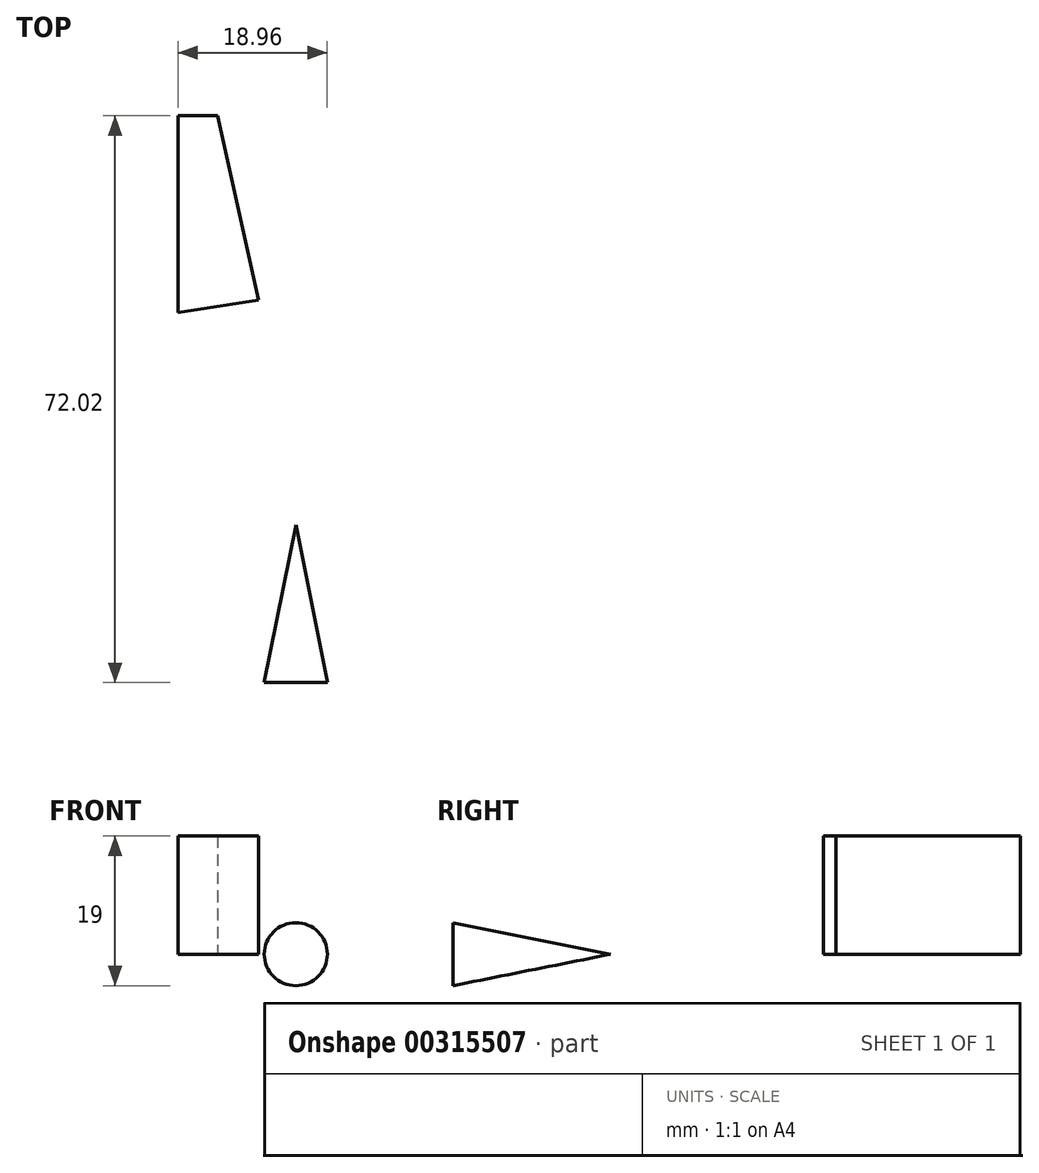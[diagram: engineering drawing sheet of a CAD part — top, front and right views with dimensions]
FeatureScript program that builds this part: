
annotation { "Feature Type Name" : "Feature", "Feature Type Description" : "" }
export const myFeature = defineFeature(function(context is Context, id is Id, definition is map)
    precondition{}
    {
        {
            var Q0;
            Q0=qCreatedBy(makeId("Top.planeOp"),FACE);
            var sketch = newSketch(context, id + "F0", { "sketchPlane" : qUnion([Q0])});
            skLineSegment(sketch, "E0", {"start": v(-41.16, -17.84) * mm, "end": v(-37.16, -17.84) * mm});
            skLineSegment(sketch, "E1", {"start": v(-37.16, -17.84) * mm, "end": v(-37.16, 2.16) * mm});
            skLineSegment(sketch, "E2", {"start": v(-37.16, 2.16) * mm, "end": v(-41.16, -17.84) * mm});
            skSolve(sketch);
        }
        {
            var Q0;
            Q0=makeQuery(id+"F0.imprint","IMPRINT",FACE,{"disambiguationData":[TD([[makeQuery(id+"F0.imprint","IMPRINT",EDGE,{"derivedFrom":sQuery(id+"F0.wireOp",EDGE,"E0")}),1.0]])]});
            var Q1;
            Q1=sQuery(id+"F0.wireOp",EDGE,"E1");
            revolve(context, id + "F1", {"entities" : qUnion([Q0]), "axis" : qUnion([Q1]), "revolveType" : RevolveType.FULL});
        }
        {
            var Q0;
            Q0=qCreatedBy(makeId("Top.planeOp"),FACE);
            var sketch = newSketch(context, id + "F2", { "sketchPlane" : qUnion([Q0])});
            skLineSegment(sketch, "E3", {"start": v(-52.12, 54.18) * mm, "end": v(-52.12, 29.18) * mm});
            skLineSegment(sketch, "E4", {"start": v(-52.12, 29.18) * mm, "end": v(-41.52, 29.18) * mm});
            skLineSegment(sketch, "E5", {"start": v(-52.12, 54.18) * mm, "end": v(-47.12, 54.18) * mm});
            skLineSegment(sketch, "E6", {"start": v(-47.12, 54.18) * mm, "end": v(-41.52, 29.18) * mm});
            skLineSegment(sketch, "E7", {"start": v(-47.12, 54.18) * mm, "end": v(-41.88, 30.76) * mm});
            skLineSegment(sketch, "E8", {"start": v(-41.88, 30.76) * mm, "end": v(-52.12, 29.18) * mm});
            skSolve(sketch);
        }
        {
            var Q0;
            Q0=makeQuery(id+"F2.imprint","IMPRINT",FACE,{"disambiguationData":[TD([[makeQuery(id+"F2.imprint","IMPRINT",EDGE,{"derivedFrom":sQuery(id+"F2.wireOp",EDGE,"E3")}),1.0]])]});
            extrude(context, id + "F3", {"entities" : qUnion([Q0]), "depth" : 15 * mm});
        }
    });
